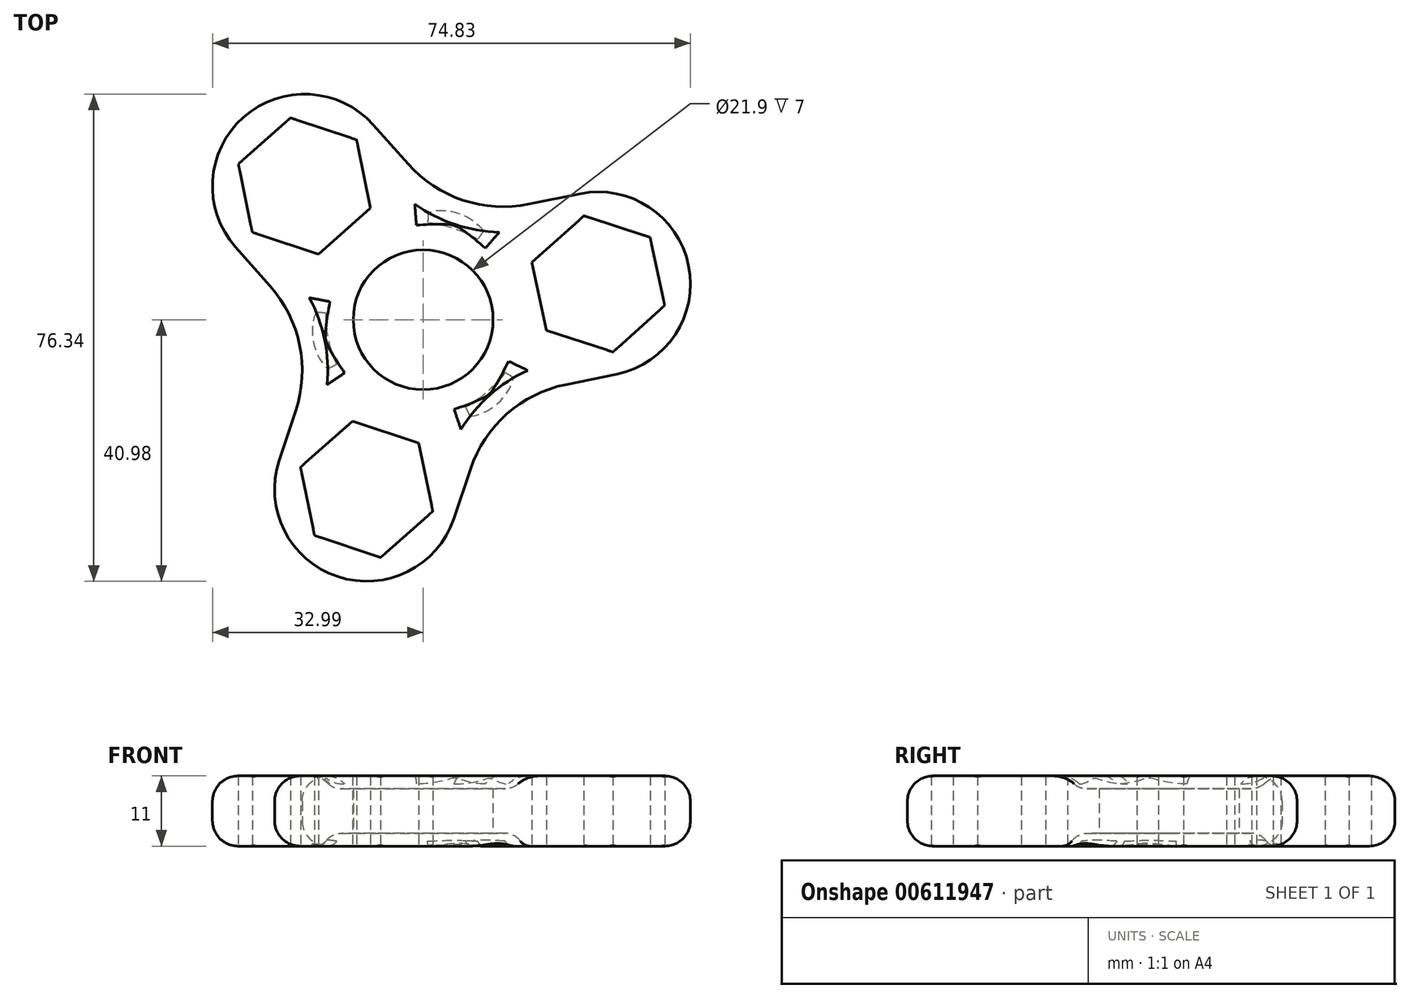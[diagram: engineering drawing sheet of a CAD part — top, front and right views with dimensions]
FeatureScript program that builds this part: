
annotation { "Feature Type Name" : "Feature", "Feature Type Description" : "" }
export const myFeature = defineFeature(function(context is Context, id is Id, definition is map)
    precondition{}
    {
        {
            var Q0;
            Q0=qCreatedBy(makeId("Top.planeOp"),FACE);
            var sketch = newSketch(context, id + "F0", { "sketchPlane" : qUnion([Q0])});
            skCircle(sketch, "E0", {"center": v(0, 0) * mm, "radius": 10.95 * mm});
            skCircle(sketch, "E1.0", {"center": v(0, 0) * mm, "radius": 14.45 * mm});
            skCircle(sketch, "E2.cCircle", {"center": v(0, 0) * mm, "radius": 14 * mm, "construction": true});
            skLineSegment(sketch, "E2.0", {"start": v(-18.58, 20.95) * mm, "end": v(27.43, 5.62) * mm, "construction": true});
            skLineSegment(sketch, "E2.1", {"start": v(27.43, 5.62) * mm, "end": v(-8.85, -26.56) * mm, "construction": true});
            skLineSegment(sketch, "E2.2", {"start": v(-8.85, -26.56) * mm, "end": v(-18.58, 20.95) * mm, "construction": true});
            skPoint(sketch, "E2.0.midPoint", {"position": v(4.43, 13.28) * mm});
            skCircle(sketch, "E3.cCircle", {"center": v(-18.58, 20.95) * mm, "radius": 9.45 * mm, "construction": true});
            skLineSegment(sketch, "E3.0", {"start": v(-28.93, 24.4) * mm, "end": v(-20.76, 31.64) * mm});
            skLineSegment(sketch, "E3.1", {"start": v(-20.76, 31.64) * mm, "end": v(-10.41, 28.18) * mm});
            skLineSegment(sketch, "E3.2", {"start": v(-10.41, 28.18) * mm, "end": v(-8.23, 17.5) * mm});
            skLineSegment(sketch, "E3.3", {"start": v(-8.23, 17.5) * mm, "end": v(-16.4, 10.26) * mm});
            skLineSegment(sketch, "E3.4", {"start": v(-16.4, 10.26) * mm, "end": v(-26.75, 13.71) * mm});
            skLineSegment(sketch, "E3.5", {"start": v(-26.75, 13.71) * mm, "end": v(-28.93, 24.4) * mm});
            skPoint(sketch, "E3.0.midPoint", {"position": v(-24.85, 28.02) * mm});
            skCircle(sketch, "E4.cCircle", {"center": v(27.43, 5.62) * mm, "radius": 9.45 * mm, "construction": true});
            skLineSegment(sketch, "E4.0", {"start": v(35.53, 12.93) * mm, "end": v(37.81, 2.26) * mm});
            skLineSegment(sketch, "E4.1", {"start": v(37.81, 2.26) * mm, "end": v(29.71, -5.05) * mm});
            skLineSegment(sketch, "E4.2", {"start": v(29.71, -5.05) * mm, "end": v(19.33, -1.7) * mm});
            skLineSegment(sketch, "E4.3", {"start": v(19.33, -1.7) * mm, "end": v(17.05, 8.98) * mm});
            skLineSegment(sketch, "E4.4", {"start": v(17.05, 8.98) * mm, "end": v(25.15, 16.29) * mm});
            skLineSegment(sketch, "E4.5", {"start": v(25.15, 16.29) * mm, "end": v(35.53, 12.93) * mm});
            skPoint(sketch, "E4.0.midPoint", {"position": v(36.67, 7.6) * mm});
            skCircle(sketch, "E5.cCircle", {"center": v(-8.85, -26.56) * mm, "radius": 9.45 * mm, "construction": true});
            skLineSegment(sketch, "E5.0", {"start": v(-6.67, -37.26) * mm, "end": v(-17.02, -33.8) * mm});
            skLineSegment(sketch, "E5.1", {"start": v(-17.02, -33.8) * mm, "end": v(-19.2, -23.1) * mm});
            skLineSegment(sketch, "E5.2", {"start": v(-19.2, -23.1) * mm, "end": v(-11.03, -15.87) * mm});
            skLineSegment(sketch, "E5.3", {"start": v(-11.03, -15.87) * mm, "end": v(-0.68, -19.33) * mm});
            skLineSegment(sketch, "E5.4", {"start": v(-0.68, -19.33) * mm, "end": v(1.5, -30.02) * mm});
            skLineSegment(sketch, "E5.5", {"start": v(1.5, -30.02) * mm, "end": v(-6.67, -37.26) * mm});
            skPoint(sketch, "E5.0.midPoint", {"position": v(-11.84, -35.53) * mm});
            skCircle(sketch, "E6", {"center": v(-8.85, -26.56) * mm, "radius": 14.41 * mm});
            skCircle(sketch, "E7", {"center": v(27.43, 5.62) * mm, "radius": 14.41 * mm});
            skCircle(sketch, "E8", {"center": v(-18.58, 20.95) * mm, "radius": 14.41 * mm});
            skLineSegment(sketch, "E9", {"start": v(-7.81, 30.53) * mm, "end": v(10.8, 9.6) * mm});
            skLineSegment(sketch, "E10", {"start": v(24.56, 19.74) * mm, "end": v(-2.88, 14.16) * mm});
            skLineSegment(sketch, "E11", {"start": v(-29.37, 11.4) * mm, "end": v(-10.82, -9.57) * mm});
            skLineSegment(sketch, "E12", {"start": v(-22.53, -22.03) * mm, "end": v(-13.72, 4.55) * mm});
            skPoint(sketch, "E12.endSnap0", {"position": v(-13.72, -2.8) * mm});
            skLineSegment(sketch, "E13", {"start": v(4.82, -31.14) * mm, "end": v(13.7, -4.59) * mm});
            skLineSegment(sketch, "E14", {"start": v(30.34, -8.5) * mm, "end": v(2.92, -14.15) * mm});
            skLineSegment(sketch, "E15", {"start": v(0, 0) * mm, "end": v(51.13, 10.48) * mm, "construction": true});
            skLineSegment(sketch, "E16", {"start": v(0, 0) * mm, "end": v(-32.6, 36.84) * mm, "construction": true});
            skLineSegment(sketch, "E17", {"start": v(0, 0) * mm, "end": v(-11.84, -35.53) * mm, "construction": true});
            skSolve(sketch);
        }
        {
            var Q0;
            {var subQ0=sQuery(id+"F0.wireOp",EDGE,"E11");var subQ1=sQuery(id+"F0.wireOp",EDGE,"E1.0");var subQ2=makeQuery(id+"F0.imprint","INTERSECT",VERTEX,{"derivedFrom":[subQ1,subQ0]});Q0=makeQuery(id+"F0.imprint","IMPRINT",FACE,{"disambiguationData":[TD([[makeQuery(id+"F0.imprint","IMPRINT",EDGE,{"disambiguationData":[TD([[subQ2,-1.0]])],"derivedFrom":subQ1}),-1.0]])]});}
            var Q1;
            {var subQ0=sQuery(id+"F0.wireOp",EDGE,"E9");var subQ1=sQuery(id+"F0.wireOp",EDGE,"E1.0");var subQ2=makeQuery(id+"F0.imprint","INTERSECT",VERTEX,{"derivedFrom":[subQ1,subQ0]});Q1=makeQuery(id+"F0.imprint","IMPRINT",FACE,{"disambiguationData":[TD([[makeQuery(id+"F0.imprint","IMPRINT",EDGE,{"disambiguationData":[TD([[subQ2,-1.0]])],"derivedFrom":subQ1}),-1.0]])]});}
            var Q2;
            {var subQ0=sQuery(id+"F0.wireOp",EDGE,"E9");var subQ1=sQuery(id+"F0.wireOp",EDGE,"E1.0");var subQ2=makeQuery(id+"F0.imprint","INTERSECT",VERTEX,{"derivedFrom":[subQ1,subQ0]});Q2=makeQuery(id+"F0.imprint","IMPRINT",FACE,{"disambiguationData":[TD([[makeQuery(id+"F0.imprint","IMPRINT",EDGE,{"disambiguationData":[TD([[subQ2,1.0]])],"derivedFrom":subQ1}),-1.0]])]});}
            var Q3;
            {var subQ0=sQuery(id+"F0.wireOp",EDGE,"E12");var subQ1=sQuery(id+"F0.wireOp",EDGE,"E1.0");var subQ2=makeQuery(id+"F0.imprint","INTERSECT",VERTEX,{"derivedFrom":[subQ1,subQ0]});Q3=makeQuery(id+"F0.imprint","IMPRINT",FACE,{"disambiguationData":[TD([[makeQuery(id+"F0.imprint","IMPRINT",EDGE,{"disambiguationData":[TD([[subQ2,1.0]])],"derivedFrom":subQ1}),-1.0]])]});}
            var Q4;
            {var subQ0=sQuery(id+"F0.wireOp",EDGE,"E14");var subQ1=sQuery(id+"F0.wireOp",EDGE,"E1.0");var subQ2=makeQuery(id+"F0.imprint","INTERSECT",VERTEX,{"derivedFrom":[subQ1,subQ0]});Q4=makeQuery(id+"F0.imprint","IMPRINT",FACE,{"disambiguationData":[TD([[makeQuery(id+"F0.imprint","IMPRINT",EDGE,{"disambiguationData":[TD([[subQ2,1.0]])],"derivedFrom":subQ1}),-1.0]])]});}
            var Q5;
            {var subQ0=sQuery(id+"F0.wireOp",EDGE,"E10");var subQ1=sQuery(id+"F0.wireOp",EDGE,"E1.0");var subQ2=makeQuery(id+"F0.imprint","INTERSECT",VERTEX,{"derivedFrom":[subQ1,subQ0]});Q5=makeQuery(id+"F0.imprint","IMPRINT",FACE,{"disambiguationData":[TD([[makeQuery(id+"F0.imprint","IMPRINT",EDGE,{"disambiguationData":[TD([[subQ2,-1.0]])],"derivedFrom":subQ1}),-1.0]])]});}
            var Q6;
            {var subQ0=sQuery(id+"F0.wireOp",EDGE,"E13");var subQ1=sQuery(id+"F0.wireOp",EDGE,"E1.0");var subQ2=makeQuery(id+"F0.imprint","INTERSECT",VERTEX,{"derivedFrom":[subQ1,subQ0]});Q6=makeQuery(id+"F0.imprint","IMPRINT",FACE,{"disambiguationData":[TD([[makeQuery(id+"F0.imprint","IMPRINT",EDGE,{"disambiguationData":[TD([[subQ2,1.0]])],"derivedFrom":subQ1}),-1.0]])]});}
            var Q7;
            Q7=makeQuery(id+"F0.imprint","IMPRINT",FACE,{"disambiguationData":[TD([[makeQuery(id+"F0.imprint","IMPRINT",EDGE,{"derivedFrom":sQuery(id+"F0.wireOp",EDGE,"E5.0")}),1.0]])]});
            var Q8;
            {var subQ0=sQuery(id+"F0.wireOp",EDGE,"E11");var subQ1=sQuery(id+"F0.wireOp",EDGE,"E1.0");var subQ2=makeQuery(id+"F0.imprint","INTERSECT",VERTEX,{"derivedFrom":[subQ1,subQ0]});Q8=makeQuery(id+"F0.imprint","IMPRINT",FACE,{"disambiguationData":[TD([[makeQuery(id+"F0.imprint","IMPRINT",EDGE,{"disambiguationData":[TD([[subQ2,1.0]])],"derivedFrom":subQ1}),-1.0]])]});}
            var Q9;
            {var subQ0=sQuery(id+"F0.wireOp",EDGE,"E13");var subQ1=sQuery(id+"F0.wireOp",EDGE,"E1.0");var subQ2=makeQuery(id+"F0.imprint","INTERSECT",VERTEX,{"derivedFrom":[subQ1,subQ0]});Q9=makeQuery(id+"F0.imprint","IMPRINT",FACE,{"disambiguationData":[TD([[makeQuery(id+"F0.imprint","IMPRINT",EDGE,{"disambiguationData":[TD([[subQ2,-1.0]])],"derivedFrom":subQ1}),-1.0]])]});}
            var Q10;
            Q10=makeQuery(id+"F0.imprint","IMPRINT",FACE,{"disambiguationData":[TD([[makeQuery(id+"F0.imprint","IMPRINT",EDGE,{"derivedFrom":sQuery(id+"F0.wireOp",EDGE,"E0")}),-1.0]])]});
            var Q11;
            Q11=makeQuery(id+"F0.imprint","IMPRINT",FACE,{"disambiguationData":[TD([[makeQuery(id+"F0.imprint","IMPRINT",EDGE,{"derivedFrom":sQuery(id+"F0.wireOp",EDGE,"E3.0")}),1.0]])]});
            var Q12;
            {var subQ0=sQuery(id+"F0.wireOp",EDGE,"E8");var subQ1=sQuery(id+"F0.wireOp",EDGE,"E1.0");var subQ2=makeQuery(id+"F0.imprint","INTERSECT",VERTEX,{"disambiguationData":[OD(0.0)],"derivedFrom":[subQ1,subQ0]});Q12=makeQuery(id+"F0.imprint","IMPRINT",FACE,{"disambiguationData":[TD([[makeQuery(id+"F0.imprint","IMPRINT",EDGE,{"disambiguationData":[TD([[subQ2,-1.0]])],"derivedFrom":subQ1}),1.0]])]});}
            var Q13;
            {var subQ0=sQuery(id+"F0.wireOp",EDGE,"E6");var subQ1=sQuery(id+"F0.wireOp",EDGE,"E1.0");var subQ2=makeQuery(id+"F0.imprint","INTERSECT",VERTEX,{"disambiguationData":[OD(0.0)],"derivedFrom":[subQ1,subQ0]});Q13=makeQuery(id+"F0.imprint","IMPRINT",FACE,{"disambiguationData":[TD([[makeQuery(id+"F0.imprint","IMPRINT",EDGE,{"disambiguationData":[TD([[subQ2,-1.0]])],"derivedFrom":subQ1}),1.0]])]});}
            var Q14;
            Q14=makeQuery(id+"F0.imprint","IMPRINT",FACE,{"disambiguationData":[TD([[makeQuery(id+"F0.imprint","IMPRINT",EDGE,{"derivedFrom":sQuery(id+"F0.wireOp",EDGE,"E4.0")}),1.0]])]});
            var Q15;
            {var subQ0=sQuery(id+"F0.wireOp",EDGE,"E7");var subQ1=sQuery(id+"F0.wireOp",EDGE,"E1.0");var subQ2=makeQuery(id+"F0.imprint","INTERSECT",VERTEX,{"disambiguationData":[OD(0.0)],"derivedFrom":[subQ1,subQ0]});Q15=makeQuery(id+"F0.imprint","IMPRINT",FACE,{"disambiguationData":[TD([[makeQuery(id+"F0.imprint","IMPRINT",EDGE,{"disambiguationData":[TD([[subQ2,1.0]])],"derivedFrom":subQ1}),1.0]])]});}
            extrude(context, id + "F1", {"entities" : qUnion([Q0, Q1, Q2, Q3, Q4, Q5, Q6, Q7, Q8, Q9, Q10, Q11, Q12, Q13, Q14, Q15]), "depth" : 11 * mm, "offsetDistance" : 25 * mm});
        }
        {
            var Q0;
            Q0=makeQuery(id+"F1.opExtrude","SWEPT_EDGE",EDGE,{"disambiguationData":[OSD([sQuery(id+"F0.wireOp",EDGE,"E13"),sQuery(id+"F0.wireOp",EDGE,"E14")])]});
            var Q1;
            Q1=makeQuery(id+"F1.opExtrude","SWEPT_EDGE",EDGE,{"disambiguationData":[OSD([sQuery(id+"F0.wireOp",EDGE,"E11"),sQuery(id+"F0.wireOp",EDGE,"E12")])]});
            var Q2;
            Q2=makeQuery(id+"F1.opExtrude","SWEPT_EDGE",EDGE,{"disambiguationData":[OSD([sQuery(id+"F0.wireOp",EDGE,"E9"),sQuery(id+"F0.wireOp",EDGE,"E10")])]});
            fillet(context, id + "F2", {"entities" : qUnion([Q0, Q1, Q2]), "radius" : 20 * mm, "tangentPropagation" : true, "allowEdgeOverflow" : false});
        }
        {
            var Q0;
            {var subQ0=sQuery(id+"F0.wireOp",EDGE,"E12");var subQ1=sQuery(id+"F0.wireOp",EDGE,"E11");Q0=makeQuery(id+"F2.opFillet","BLEND_EDGE",EDGE,{"blendedFrom":[makeQuery(id+"F1.opExtrude","SWEPT_EDGE",EDGE,{"disambiguationData":[OSD([subQ1,subQ0])]}),makeQuery(id+"F1.opExtrude","CAP_FACE",FACE,{"disambiguationData":[OSD([sQuery(id+"F0.wireOp",EDGE,"E1.0"),sQuery(id+"F0.wireOp",EDGE,"E3.0"),sQuery(id+"F0.wireOp",EDGE,"E3.1"),sQuery(id+"F0.wireOp",EDGE,"E3.2"),sQuery(id+"F0.wireOp",EDGE,"E3.3"),sQuery(id+"F0.wireOp",EDGE,"E3.4"),sQuery(id+"F0.wireOp",EDGE,"E3.5"),sQuery(id+"F0.wireOp",EDGE,"E4.0"),sQuery(id+"F0.wireOp",EDGE,"E4.1"),sQuery(id+"F0.wireOp",EDGE,"E4.2"),sQuery(id+"F0.wireOp",EDGE,"E4.3"),sQuery(id+"F0.wireOp",EDGE,"E4.4"),sQuery(id+"F0.wireOp",EDGE,"E4.5"),sQuery(id+"F0.wireOp",EDGE,"E5.0"),sQuery(id+"F0.wireOp",EDGE,"E5.1"),sQuery(id+"F0.wireOp",EDGE,"E5.2"),sQuery(id+"F0.wireOp",EDGE,"E5.3"),sQuery(id+"F0.wireOp",EDGE,"E5.4"),sQuery(id+"F0.wireOp",EDGE,"E5.5"),sQuery(id+"F0.wireOp",EDGE,"E6"),sQuery(id+"F0.wireOp",EDGE,"E7"),sQuery(id+"F0.wireOp",EDGE,"E8"),sQuery(id+"F0.wireOp",EDGE,"E9"),sQuery(id+"F0.wireOp",EDGE,"E10"),subQ1,subQ0,sQuery(id+"F0.wireOp",EDGE,"E13"),sQuery(id+"F0.wireOp",EDGE,"E14")])],"isStart":false})],"blendedInto":[makeQuery(id+"F1.opExtrude","CAP_FACE",FACE,{"disambiguationData":[OSD([sQuery(id+"F0.wireOp",EDGE,"E1.0"),sQuery(id+"F0.wireOp",EDGE,"E3.0"),sQuery(id+"F0.wireOp",EDGE,"E3.1"),sQuery(id+"F0.wireOp",EDGE,"E3.2"),sQuery(id+"F0.wireOp",EDGE,"E3.3"),sQuery(id+"F0.wireOp",EDGE,"E3.4"),sQuery(id+"F0.wireOp",EDGE,"E3.5"),sQuery(id+"F0.wireOp",EDGE,"E4.0"),sQuery(id+"F0.wireOp",EDGE,"E4.1"),sQuery(id+"F0.wireOp",EDGE,"E4.2"),sQuery(id+"F0.wireOp",EDGE,"E4.3"),sQuery(id+"F0.wireOp",EDGE,"E4.4"),sQuery(id+"F0.wireOp",EDGE,"E4.5"),sQuery(id+"F0.wireOp",EDGE,"E5.0"),sQuery(id+"F0.wireOp",EDGE,"E5.1"),sQuery(id+"F0.wireOp",EDGE,"E5.2"),sQuery(id+"F0.wireOp",EDGE,"E5.3"),sQuery(id+"F0.wireOp",EDGE,"E5.4"),sQuery(id+"F0.wireOp",EDGE,"E5.5"),sQuery(id+"F0.wireOp",EDGE,"E6"),sQuery(id+"F0.wireOp",EDGE,"E7"),sQuery(id+"F0.wireOp",EDGE,"E8"),sQuery(id+"F0.wireOp",EDGE,"E9"),sQuery(id+"F0.wireOp",EDGE,"E10"),subQ1,subQ0,sQuery(id+"F0.wireOp",EDGE,"E13"),sQuery(id+"F0.wireOp",EDGE,"E14")])],"isStart":false})]});}
            var Q1;
            {var subQ0=sQuery(id+"F0.wireOp",EDGE,"E12");var subQ1=sQuery(id+"F0.wireOp",EDGE,"E11");Q1=makeQuery(id+"F2.opFillet","BLEND_EDGE",EDGE,{"blendedFrom":[makeQuery(id+"F1.opExtrude","SWEPT_EDGE",EDGE,{"disambiguationData":[OSD([subQ1,subQ0])]}),makeQuery(id+"F1.opExtrude","CAP_FACE",FACE,{"disambiguationData":[OSD([sQuery(id+"F0.wireOp",EDGE,"E1.0"),sQuery(id+"F0.wireOp",EDGE,"E3.0"),sQuery(id+"F0.wireOp",EDGE,"E3.1"),sQuery(id+"F0.wireOp",EDGE,"E3.2"),sQuery(id+"F0.wireOp",EDGE,"E3.3"),sQuery(id+"F0.wireOp",EDGE,"E3.4"),sQuery(id+"F0.wireOp",EDGE,"E3.5"),sQuery(id+"F0.wireOp",EDGE,"E4.0"),sQuery(id+"F0.wireOp",EDGE,"E4.1"),sQuery(id+"F0.wireOp",EDGE,"E4.2"),sQuery(id+"F0.wireOp",EDGE,"E4.3"),sQuery(id+"F0.wireOp",EDGE,"E4.4"),sQuery(id+"F0.wireOp",EDGE,"E4.5"),sQuery(id+"F0.wireOp",EDGE,"E5.0"),sQuery(id+"F0.wireOp",EDGE,"E5.1"),sQuery(id+"F0.wireOp",EDGE,"E5.2"),sQuery(id+"F0.wireOp",EDGE,"E5.3"),sQuery(id+"F0.wireOp",EDGE,"E5.4"),sQuery(id+"F0.wireOp",EDGE,"E5.5"),sQuery(id+"F0.wireOp",EDGE,"E6"),sQuery(id+"F0.wireOp",EDGE,"E7"),sQuery(id+"F0.wireOp",EDGE,"E8"),sQuery(id+"F0.wireOp",EDGE,"E9"),sQuery(id+"F0.wireOp",EDGE,"E10"),subQ1,subQ0,sQuery(id+"F0.wireOp",EDGE,"E13"),sQuery(id+"F0.wireOp",EDGE,"E14")])],"isStart":true})],"blendedInto":[makeQuery(id+"F1.opExtrude","CAP_FACE",FACE,{"disambiguationData":[OSD([sQuery(id+"F0.wireOp",EDGE,"E1.0"),sQuery(id+"F0.wireOp",EDGE,"E3.0"),sQuery(id+"F0.wireOp",EDGE,"E3.1"),sQuery(id+"F0.wireOp",EDGE,"E3.2"),sQuery(id+"F0.wireOp",EDGE,"E3.3"),sQuery(id+"F0.wireOp",EDGE,"E3.4"),sQuery(id+"F0.wireOp",EDGE,"E3.5"),sQuery(id+"F0.wireOp",EDGE,"E4.0"),sQuery(id+"F0.wireOp",EDGE,"E4.1"),sQuery(id+"F0.wireOp",EDGE,"E4.2"),sQuery(id+"F0.wireOp",EDGE,"E4.3"),sQuery(id+"F0.wireOp",EDGE,"E4.4"),sQuery(id+"F0.wireOp",EDGE,"E4.5"),sQuery(id+"F0.wireOp",EDGE,"E5.0"),sQuery(id+"F0.wireOp",EDGE,"E5.1"),sQuery(id+"F0.wireOp",EDGE,"E5.2"),sQuery(id+"F0.wireOp",EDGE,"E5.3"),sQuery(id+"F0.wireOp",EDGE,"E5.4"),sQuery(id+"F0.wireOp",EDGE,"E5.5"),sQuery(id+"F0.wireOp",EDGE,"E6"),sQuery(id+"F0.wireOp",EDGE,"E7"),sQuery(id+"F0.wireOp",EDGE,"E8"),sQuery(id+"F0.wireOp",EDGE,"E9"),sQuery(id+"F0.wireOp",EDGE,"E10"),subQ1,subQ0,sQuery(id+"F0.wireOp",EDGE,"E13"),sQuery(id+"F0.wireOp",EDGE,"E14")])],"isStart":true})]});}
            fillet(context, id + "F3", {"entities" : qUnion([Q0, Q1]), "radius" : 4 * mm, "tangentPropagation" : true, "allowEdgeOverflow" : false});
        }
        {
            var Q0;
            Q0=makeQuery(id+"F0.imprint","IMPRINT",FACE,{"disambiguationData":[TD([[makeQuery(id+"F0.imprint","IMPRINT",EDGE,{"derivedFrom":sQuery(id+"F0.wireOp",EDGE,"E0")}),1.0]])]});
            var sketch = newSketch(context, id + "F4", { "sketchPlane" : qUnion([Q0])});
            skCircle(sketch, "E18", {"center": v(0, 0) * mm, "radius": 15.65 * mm});
            skSolve(sketch);
        }
        {
            var Q0;
            Q0 = qSketchRegion(id + "F4", true);
            extrude(context, id + "F5", {"entities" : qUnion([Q0]), "operationType" : NewBodyOperationType.REMOVE, "depth" : 2 * mm, "offsetDistance" : 25 * mm});
        }
        {
            var Q0;
            Q0=makeQuery(id+"F5.boolean.opBoolean","COPY",EDGE,{"derivedFrom":makeQuery(id+"F5.opExtrude","CAP_EDGE",EDGE,{"disambiguationData":[OSD([sQuery(id+"F4.wireOp",EDGE,"E18")])],"isStart":false})});
            fillet(context, id + "F6", {"entities" : qUnion([Q0]), "radius" : 3 * mm, "tangentPropagation" : true, "allowEdgeOverflow" : false});
        }
        {
            var Q0;
            Q0=makeQuery(id+"F3.opFillet","SPLIT",FACE,{"disambiguationData":[OD(0.0)],"derivedFrom":makeQuery(id+"F1.opExtrude","CAP_FACE",FACE,{"disambiguationData":[OSD([sQuery(id+"F0.wireOp",EDGE,"E0"),sQuery(id+"F0.wireOp",EDGE,"E3.0"),sQuery(id+"F0.wireOp",EDGE,"E3.1"),sQuery(id+"F0.wireOp",EDGE,"E3.2"),sQuery(id+"F0.wireOp",EDGE,"E3.3"),sQuery(id+"F0.wireOp",EDGE,"E3.4"),sQuery(id+"F0.wireOp",EDGE,"E3.5"),sQuery(id+"F0.wireOp",EDGE,"E4.0"),sQuery(id+"F0.wireOp",EDGE,"E4.1"),sQuery(id+"F0.wireOp",EDGE,"E4.2"),sQuery(id+"F0.wireOp",EDGE,"E4.3"),sQuery(id+"F0.wireOp",EDGE,"E4.4"),sQuery(id+"F0.wireOp",EDGE,"E4.5"),sQuery(id+"F0.wireOp",EDGE,"E5.0"),sQuery(id+"F0.wireOp",EDGE,"E5.1"),sQuery(id+"F0.wireOp",EDGE,"E5.2"),sQuery(id+"F0.wireOp",EDGE,"E5.3"),sQuery(id+"F0.wireOp",EDGE,"E5.4"),sQuery(id+"F0.wireOp",EDGE,"E5.5"),sQuery(id+"F0.wireOp",EDGE,"E6"),sQuery(id+"F0.wireOp",EDGE,"E7"),sQuery(id+"F0.wireOp",EDGE,"E8"),sQuery(id+"F0.wireOp",EDGE,"E9"),sQuery(id+"F0.wireOp",EDGE,"E10"),sQuery(id+"F0.wireOp",EDGE,"E11"),sQuery(id+"F0.wireOp",EDGE,"E12"),sQuery(id+"F0.wireOp",EDGE,"E13"),sQuery(id+"F0.wireOp",EDGE,"E14")])],"isStart":false})});
            var sketch = newSketch(context, id + "F7", { "sketchPlane" : qUnion([Q0])});
            skCircle(sketch, "E19", {"center": v(0, 0) * mm, "radius": 15.7 * mm});
            skSolve(sketch);
        }
        {
            var Q0;
            Q0 = qSketchRegion(id + "F7", true);
            extrude(context, id + "F8", {"entities" : qUnion([Q0]), "operationType" : NewBodyOperationType.REMOVE, "oppositeDirection" : true, "depth" : 2 * mm, "offsetDistance" : 25 * mm});
        }
        {
            var Q0;
            Q0=makeQuery(id+"F8.boolean.opBoolean","COPY",EDGE,{"derivedFrom":makeQuery(id+"F8.opExtrude","CAP_EDGE",EDGE,{"disambiguationData":[OSD([sQuery(id+"F7.wireOp",EDGE,"E19")])],"isStart":false})});
            fillet(context, id + "F9", {"entities" : qUnion([Q0]), "radius" : 3 * mm, "tangentPropagation" : true, "allowEdgeOverflow" : false});
        }
        {
            var Q0;
            Q0=makeQuery(id+"F9.opFillet","BLEND_EDGE",EDGE,{"blendedFrom":[makeQuery(id+"F8.boolean.opBoolean","COPY",EDGE,{"derivedFrom":makeQuery(id+"F8.opExtrude","CAP_EDGE",EDGE,{"disambiguationData":[OSD([sQuery(id+"F7.wireOp",EDGE,"E19")])],"isStart":false})}),makeQuery(id+"F3.opFillet","SPLIT",FACE,{"disambiguationData":[OD(0.0)],"derivedFrom":makeQuery(id+"F1.opExtrude","CAP_FACE",FACE,{"disambiguationData":[OSD([sQuery(id+"F0.wireOp",EDGE,"E0"),sQuery(id+"F0.wireOp",EDGE,"E3.0"),sQuery(id+"F0.wireOp",EDGE,"E3.1"),sQuery(id+"F0.wireOp",EDGE,"E3.2"),sQuery(id+"F0.wireOp",EDGE,"E3.3"),sQuery(id+"F0.wireOp",EDGE,"E3.4"),sQuery(id+"F0.wireOp",EDGE,"E3.5"),sQuery(id+"F0.wireOp",EDGE,"E4.0"),sQuery(id+"F0.wireOp",EDGE,"E4.1"),sQuery(id+"F0.wireOp",EDGE,"E4.2"),sQuery(id+"F0.wireOp",EDGE,"E4.3"),sQuery(id+"F0.wireOp",EDGE,"E4.4"),sQuery(id+"F0.wireOp",EDGE,"E4.5"),sQuery(id+"F0.wireOp",EDGE,"E5.0"),sQuery(id+"F0.wireOp",EDGE,"E5.1"),sQuery(id+"F0.wireOp",EDGE,"E5.2"),sQuery(id+"F0.wireOp",EDGE,"E5.3"),sQuery(id+"F0.wireOp",EDGE,"E5.4"),sQuery(id+"F0.wireOp",EDGE,"E5.5"),sQuery(id+"F0.wireOp",EDGE,"E6"),sQuery(id+"F0.wireOp",EDGE,"E7"),sQuery(id+"F0.wireOp",EDGE,"E8"),sQuery(id+"F0.wireOp",EDGE,"E9"),sQuery(id+"F0.wireOp",EDGE,"E10"),sQuery(id+"F0.wireOp",EDGE,"E11"),sQuery(id+"F0.wireOp",EDGE,"E12"),sQuery(id+"F0.wireOp",EDGE,"E13"),sQuery(id+"F0.wireOp",EDGE,"E14")])],"isStart":false})})],"blendedInto":[makeQuery(id+"F3.opFillet","SPLIT",FACE,{"disambiguationData":[OD(0.0)],"derivedFrom":makeQuery(id+"F1.opExtrude","CAP_FACE",FACE,{"disambiguationData":[OSD([sQuery(id+"F0.wireOp",EDGE,"E0"),sQuery(id+"F0.wireOp",EDGE,"E3.0"),sQuery(id+"F0.wireOp",EDGE,"E3.1"),sQuery(id+"F0.wireOp",EDGE,"E3.2"),sQuery(id+"F0.wireOp",EDGE,"E3.3"),sQuery(id+"F0.wireOp",EDGE,"E3.4"),sQuery(id+"F0.wireOp",EDGE,"E3.5"),sQuery(id+"F0.wireOp",EDGE,"E4.0"),sQuery(id+"F0.wireOp",EDGE,"E4.1"),sQuery(id+"F0.wireOp",EDGE,"E4.2"),sQuery(id+"F0.wireOp",EDGE,"E4.3"),sQuery(id+"F0.wireOp",EDGE,"E4.4"),sQuery(id+"F0.wireOp",EDGE,"E4.5"),sQuery(id+"F0.wireOp",EDGE,"E5.0"),sQuery(id+"F0.wireOp",EDGE,"E5.1"),sQuery(id+"F0.wireOp",EDGE,"E5.2"),sQuery(id+"F0.wireOp",EDGE,"E5.3"),sQuery(id+"F0.wireOp",EDGE,"E5.4"),sQuery(id+"F0.wireOp",EDGE,"E5.5"),sQuery(id+"F0.wireOp",EDGE,"E6"),sQuery(id+"F0.wireOp",EDGE,"E7"),sQuery(id+"F0.wireOp",EDGE,"E8"),sQuery(id+"F0.wireOp",EDGE,"E9"),sQuery(id+"F0.wireOp",EDGE,"E10"),sQuery(id+"F0.wireOp",EDGE,"E11"),sQuery(id+"F0.wireOp",EDGE,"E12"),sQuery(id+"F0.wireOp",EDGE,"E13"),sQuery(id+"F0.wireOp",EDGE,"E14")])],"isStart":false})})]});
            fillet(context, id + "F10", {"entities" : qUnion([Q0]), "radius" : 5 * mm, "tangentPropagation" : true, "allowEdgeOverflow" : false});
        }
        {
            var Q0;
            Q0=makeQuery(id+"F6.opFillet","BLEND_EDGE",EDGE,{"blendedFrom":[makeQuery(id+"F5.boolean.opBoolean","COPY",EDGE,{"derivedFrom":makeQuery(id+"F5.opExtrude","CAP_EDGE",EDGE,{"disambiguationData":[OSD([sQuery(id+"F4.wireOp",EDGE,"E18")])],"isStart":false})}),makeQuery(id+"F3.opFillet","SPLIT",FACE,{"disambiguationData":[OD(0.0)],"derivedFrom":makeQuery(id+"F1.opExtrude","CAP_FACE",FACE,{"disambiguationData":[OSD([sQuery(id+"F0.wireOp",EDGE,"E0"),sQuery(id+"F0.wireOp",EDGE,"E3.0"),sQuery(id+"F0.wireOp",EDGE,"E3.1"),sQuery(id+"F0.wireOp",EDGE,"E3.2"),sQuery(id+"F0.wireOp",EDGE,"E3.3"),sQuery(id+"F0.wireOp",EDGE,"E3.4"),sQuery(id+"F0.wireOp",EDGE,"E3.5"),sQuery(id+"F0.wireOp",EDGE,"E4.0"),sQuery(id+"F0.wireOp",EDGE,"E4.1"),sQuery(id+"F0.wireOp",EDGE,"E4.2"),sQuery(id+"F0.wireOp",EDGE,"E4.3"),sQuery(id+"F0.wireOp",EDGE,"E4.4"),sQuery(id+"F0.wireOp",EDGE,"E4.5"),sQuery(id+"F0.wireOp",EDGE,"E5.0"),sQuery(id+"F0.wireOp",EDGE,"E5.1"),sQuery(id+"F0.wireOp",EDGE,"E5.2"),sQuery(id+"F0.wireOp",EDGE,"E5.3"),sQuery(id+"F0.wireOp",EDGE,"E5.4"),sQuery(id+"F0.wireOp",EDGE,"E5.5"),sQuery(id+"F0.wireOp",EDGE,"E6"),sQuery(id+"F0.wireOp",EDGE,"E7"),sQuery(id+"F0.wireOp",EDGE,"E8"),sQuery(id+"F0.wireOp",EDGE,"E9"),sQuery(id+"F0.wireOp",EDGE,"E10"),sQuery(id+"F0.wireOp",EDGE,"E11"),sQuery(id+"F0.wireOp",EDGE,"E12"),sQuery(id+"F0.wireOp",EDGE,"E13"),sQuery(id+"F0.wireOp",EDGE,"E14")])],"isStart":true})})],"blendedInto":[makeQuery(id+"F3.opFillet","SPLIT",FACE,{"disambiguationData":[OD(0.0)],"derivedFrom":makeQuery(id+"F1.opExtrude","CAP_FACE",FACE,{"disambiguationData":[OSD([sQuery(id+"F0.wireOp",EDGE,"E0"),sQuery(id+"F0.wireOp",EDGE,"E3.0"),sQuery(id+"F0.wireOp",EDGE,"E3.1"),sQuery(id+"F0.wireOp",EDGE,"E3.2"),sQuery(id+"F0.wireOp",EDGE,"E3.3"),sQuery(id+"F0.wireOp",EDGE,"E3.4"),sQuery(id+"F0.wireOp",EDGE,"E3.5"),sQuery(id+"F0.wireOp",EDGE,"E4.0"),sQuery(id+"F0.wireOp",EDGE,"E4.1"),sQuery(id+"F0.wireOp",EDGE,"E4.2"),sQuery(id+"F0.wireOp",EDGE,"E4.3"),sQuery(id+"F0.wireOp",EDGE,"E4.4"),sQuery(id+"F0.wireOp",EDGE,"E4.5"),sQuery(id+"F0.wireOp",EDGE,"E5.0"),sQuery(id+"F0.wireOp",EDGE,"E5.1"),sQuery(id+"F0.wireOp",EDGE,"E5.2"),sQuery(id+"F0.wireOp",EDGE,"E5.3"),sQuery(id+"F0.wireOp",EDGE,"E5.4"),sQuery(id+"F0.wireOp",EDGE,"E5.5"),sQuery(id+"F0.wireOp",EDGE,"E6"),sQuery(id+"F0.wireOp",EDGE,"E7"),sQuery(id+"F0.wireOp",EDGE,"E8"),sQuery(id+"F0.wireOp",EDGE,"E9"),sQuery(id+"F0.wireOp",EDGE,"E10"),sQuery(id+"F0.wireOp",EDGE,"E11"),sQuery(id+"F0.wireOp",EDGE,"E12"),sQuery(id+"F0.wireOp",EDGE,"E13"),sQuery(id+"F0.wireOp",EDGE,"E14")])],"isStart":true})})]});
            fillet(context, id + "F11", {"entities" : qUnion([Q0]), "radius" : 2 * mm, "tangentPropagation" : true, "allowEdgeOverflow" : false});
        }
    });
